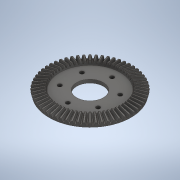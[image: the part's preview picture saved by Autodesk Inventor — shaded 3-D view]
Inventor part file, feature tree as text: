
AUTODESK INVENTOR PART (.ipt)
format: ipt  version: 2020 (Build 240168000, 168)  size: 2,778,624 bytes
history: native  units: in
note: dims shown in document units (in); Inventor stores cm internally (conversion verified against a paired STEP export)
features: extrude x2, sketch x2, imported_body x1
ambient origin geometry x8: Origin, YZ Plane, XZ Plane, XY Plane, X Axis, Y Axis, Z Axis, Center Point
bodies: Solid1 (feature_tree)
feature tree (5):
  extrude  "Extrusion1"  Depth=0.9375in
  extrude  "Extrusion2"  Depth=0.17in
  sketch  "Sketch1"  dims[d0=0.685in d1=0.0in d3=0.9375in]
  sketch  "Sketch2"  dims[d4=1.125in d5=0.17in d6=2.3622in d8=360.0deg d10=0.685in d11=0.0in]
  imported_body  "Base1"
